# Revit family: Connection-Cleat Plate-Steel & Tube-HST Standard
name_source: partatom
category: Structural Connections
revit_build: Autodesk Revit 2017 (Build: 20170118_1100(x64)
units: mm (PartAtom-declared; Revit-internal decimal feet)

## family parameters
Cut with Voids When Loaded = No
Enable cutting in views = Yes
Host = Face
Material for Model Behavior = Steel
OmniClass Number = 23.25.05.17.11
OmniClass Title = Column Bases
Shared = Yes

## types (7) — shared parameters
Assembly Code = B1020230
CBICode = 3411
CBIDescription = Structural steelwork
Description = HST Steel Purlins and Girts are high strength lipped profile sections, providing an economic solution for your building project.
Design Instruction = All the design information should be cross referenced with the current Steel & Tube Purlins and Girts design guide, and AS/NZS 4600:2005
Design Standard = Steel & Tube’s HST purlins and Girts profiles are designed in accordance with AS/NZS 4600:2005.
Length_ANZRS = 8 mm  [stored 0.0262467 ft]
Manufacturer = Steel & Tube
ManufacturerName = Steel & Tube
ManufacturerURL = http://www.steelandtube.co.nz
Material Standard = Steel & Tube’s HST purlins and Girts profiles are manufactured from materials conforming to AS1397:2011
Material_ANZRS = Metal-Steel-450MPa
ModifiedIssue_ANZRS = 20160520 $
PlateThickness_ANZRS = 8 mm  [stored 0.0262467 ft]
SpecificationDescription = Steel & Tube Purlins & Girts
SpecificationReference = 3411ST
Type Comments = HST Steel Purlin Standard Cleat
URL = http://www.steelandtube.co.nz
Uniclass2015Code = Pr_20_76_51_21
Uniclass2015Title = Cold-formed galvanized steel sections
Uniclass2015Version = 2015
zero-valued in all types: Default Elevation

## per-type parameters (varying)
| type | Beam Size | Bolt Row2 Validation | Height_ANZRS | f | g |
| HST100 | 102 mm | 500 mm  [stored 1.64042 ft] | 100 mm  [stored 0.328084 ft] | 57 mm  [stored 0.187008 ft] | 64 mm  [stored 0.209974 ft] |
| HST150 | 152 mm  [stored 0.498688 ft] | 80 mm  [stored 0.262467 ft] | 150 mm | 41 mm  [stored 0.134514 ft] | 80 mm  [stored 0.262467 ft] |
| HST200 | 203 mm  [stored 0.66601 ft] | 120 mm  [stored 0.393701 ft] | 200 mm  [stored 0.656168 ft] | 48 mm  [stored 0.15748 ft] | 120 mm  [stored 0.393701 ft] |
| HST250 | 250 mm  [stored 0.82021 ft] | 160 mm  [stored 0.524934 ft] | 250 mm  [stored 0.82021 ft] | 53 mm  [stored 0.173885 ft] | 160 mm  [stored 0.524934 ft] |
| HST300 | 300 mm | 200 mm  [stored 0.656168 ft] | 300 mm | 55 mm  [stored 0.180446 ft] | 200 mm  [stored 0.656168 ft] |
| HST350 | 350 mm  [stored 1.14829 ft] | 240 mm  [stored 0.787402 ft] | 340 mm  [stored 1.11549 ft] | 60 mm  [stored 0.19685 ft] | 240 mm  [stored 0.787402 ft] |
| HST400 | 400 mm | 280 mm  [stored 0.918635 ft] | 380 mm | 70 mm  [stored 0.229659 ft] | 280 mm  [stored 0.918635 ft] |

note: column(s) folded — value = type name in every type: Model

note: [stored X ft] marks values corroborated as IEEE doubles in the binary element streams (Revit-internal decimal feet)

## geometry (parser evidence)
native form markers: Sweep x2
no freeform markers — native parametric forms only
